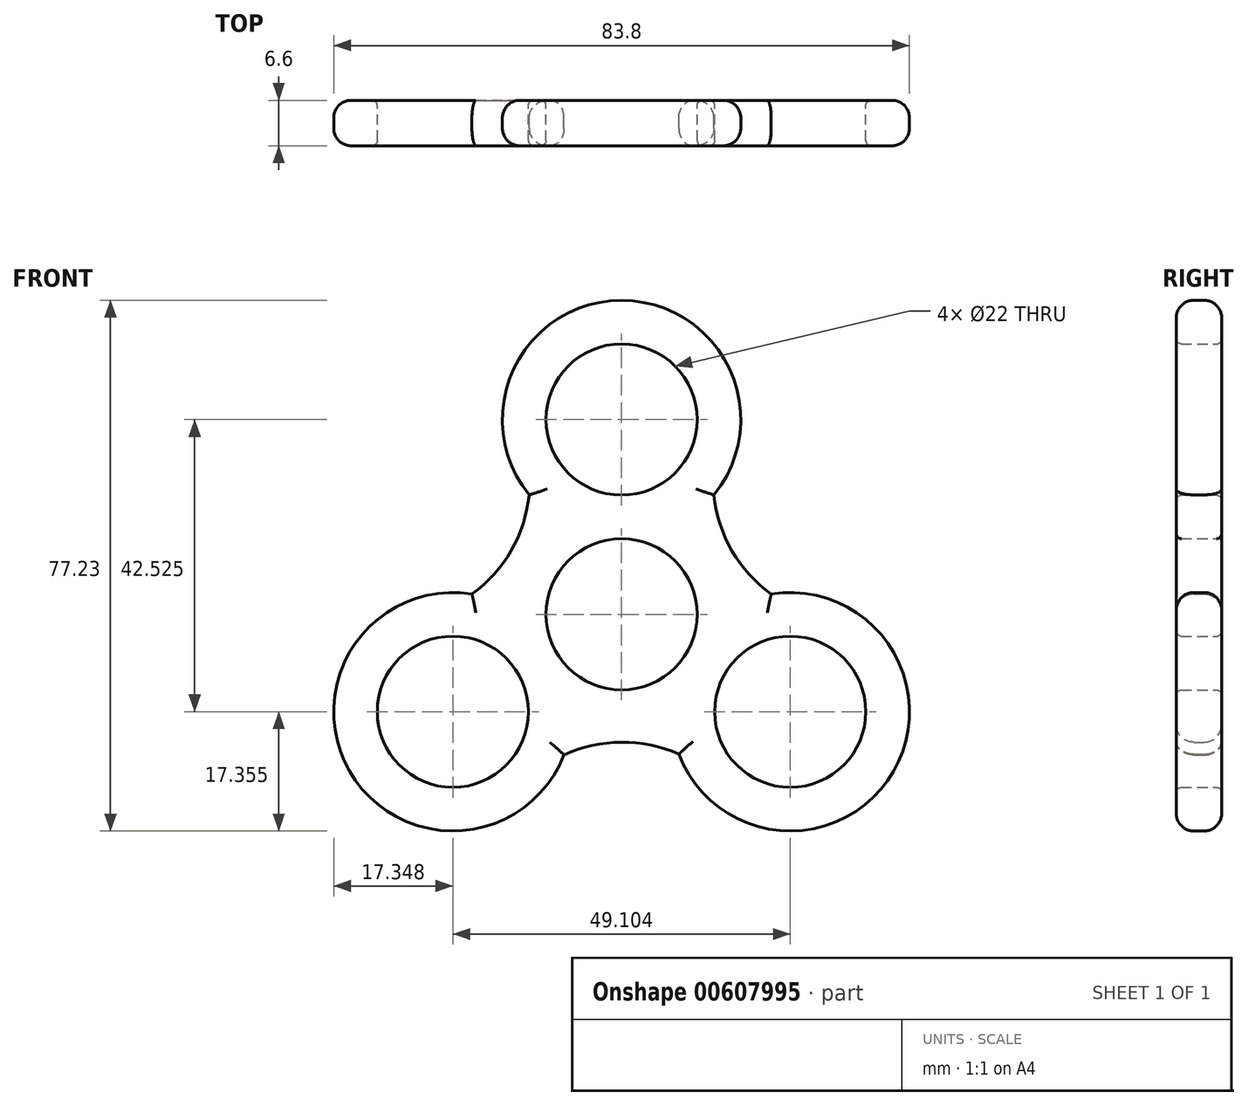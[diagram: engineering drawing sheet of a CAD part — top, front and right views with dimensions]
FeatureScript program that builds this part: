
annotation { "Feature Type Name" : "Feature", "Feature Type Description" : "" }
export const myFeature = defineFeature(function(context is Context, id is Id, definition is map)
    precondition{}
    {
        {
            var Q0;
            Q0=qCreatedBy(makeId("Front.planeOp"),FACE);
            var sketch = newSketch(context, id + "F0", { "sketchPlane" : qUnion([Q0])});
            skCircle(sketch, "E0", {"center": v(0, 0) * mm, "radius": 11 * mm});
            skCircle(sketch, "E1", {"center": v(0, 28.35) * mm, "radius": 11 * mm});
            skCircle(sketch, "E2", {"center": v(24.55, -14.17) * mm, "radius": 11 * mm});
            skCircle(sketch, "E3", {"center": v(-24.55, -14.18) * mm, "radius": 11 * mm});
            skArc(sketch, "E4", {"start": v(13.45, 17.39) * mm, "mid": v(0, 45.7) * mm, "end": v(-13.45, 17.39) * mm});
            skArc(sketch, "E5", {"start": v(8.33, -20.34) * mm, "mid": v(39.58, -22.85) * mm, "end": v(21.78, 2.95) * mm});
            skArc(sketch, "E6", {"start": v(-21.78, 2.95) * mm, "mid": v(-39.6, -22.8) * mm, "end": v(-8.38, -20.46) * mm});
            skPoint(sketch, "E7", {"position": v(13.45, 17.39) * mm});
            skPoint(sketch, "E8", {"position": v(21.78, 2.95) * mm});
            skPoint(sketch, "E9", {"position": v(8.33, -20.34) * mm});
            skPoint(sketch, "E10", {"position": v(-8.38, -20.46) * mm});
            skPoint(sketch, "E11", {"position": v(-21.78, 2.95) * mm});
            skPoint(sketch, "E12", {"position": v(-13.45, 17.39) * mm});
            skArc(sketch, "E13", {"start": v(13.45, 17.39) * mm, "mid": v(16.07, 9.28) * mm, "end": v(21.78, 2.95) * mm});
            skArc(sketch, "E14", {"start": v(8.33, -20.34) * mm, "mid": v(-0.03, -18.6) * mm, "end": v(-8.38, -20.46) * mm});
            skArc(sketch, "E15", {"start": v(-21.78, 2.95) * mm, "mid": v(-16.07, 9.28) * mm, "end": v(-13.45, 17.39) * mm});
            skPoint(sketch, "E16.orphan", {"position": v(-9.7, 13.96) * mm});
            skPoint(sketch, "E17.orphan", {"position": v(9.7, 13.96) * mm});
            skPoint(sketch, "E18.orphan", {"position": v(-7.24, -15.38) * mm});
            skPoint(sketch, "E19.orphan", {"position": v(-16.94, 1.42) * mm});
            skPoint(sketch, "E20.orphan", {"position": v(16.94, 1.42) * mm});
            skPoint(sketch, "E21.orphan", {"position": v(7.24, -15.38) * mm});
            skSolve(sketch);
        }
        {
            var Q0;
            Q0 = qSketchRegion(id + "F0", true);
            extrude(context, id + "F1", {"entities" : qUnion([Q0]), "depth" : 6.6 * mm, "offsetDistance" : 25.4 * mm});
        }
        {
            var Q0;
            Q0=makeQuery(id+"F1.opExtrude","CAP_EDGE",EDGE,{"disambiguationData":[OSD([sQuery(id+"F0.wireOp",EDGE,"E4")])],"isStart":false});
            var Q1;
            Q1=makeQuery(id+"F1.opExtrude","CAP_EDGE",EDGE,{"disambiguationData":[OSD([sQuery(id+"F0.wireOp",EDGE,"E4")])],"isStart":true});
            var Q2;
            Q2=makeQuery(id+"F1.opExtrude","CAP_EDGE",EDGE,{"disambiguationData":[OSD([sQuery(id+"F0.wireOp",EDGE,"E13")])],"isStart":false});
            var Q3;
            Q3=makeQuery(id+"F1.opExtrude","CAP_EDGE",EDGE,{"disambiguationData":[OSD([sQuery(id+"F0.wireOp",EDGE,"E15")])],"isStart":false});
            var Q4;
            Q4=makeQuery(id+"F1.opExtrude","CAP_EDGE",EDGE,{"disambiguationData":[OSD([sQuery(id+"F0.wireOp",EDGE,"E6")])],"isStart":false});
            var Q5;
            Q5=makeQuery(id+"F1.opExtrude","CAP_EDGE",EDGE,{"disambiguationData":[OSD([sQuery(id+"F0.wireOp",EDGE,"E14")])],"isStart":false});
            var Q6;
            Q6=makeQuery(id+"F1.opExtrude","CAP_EDGE",EDGE,{"disambiguationData":[OSD([sQuery(id+"F0.wireOp",EDGE,"E5")])],"isStart":false});
            var Q7;
            Q7=makeQuery(id+"F1.opExtrude","CAP_EDGE",EDGE,{"disambiguationData":[OSD([sQuery(id+"F0.wireOp",EDGE,"E13")])],"isStart":true});
            var Q8;
            Q8=makeQuery(id+"F1.opExtrude","CAP_EDGE",EDGE,{"disambiguationData":[OSD([sQuery(id+"F0.wireOp",EDGE,"E15")])],"isStart":true});
            var Q9;
            Q9=makeQuery(id+"F1.opExtrude","CAP_EDGE",EDGE,{"disambiguationData":[OSD([sQuery(id+"F0.wireOp",EDGE,"E6")])],"isStart":true});
            var Q10;
            Q10=makeQuery(id+"F1.opExtrude","CAP_EDGE",EDGE,{"disambiguationData":[OSD([sQuery(id+"F0.wireOp",EDGE,"E14")])],"isStart":true});
            var Q11;
            Q11=makeQuery(id+"F1.opExtrude","CAP_EDGE",EDGE,{"disambiguationData":[OSD([sQuery(id+"F0.wireOp",EDGE,"E5")])],"isStart":true});
            fillet(context, id + "F2", {"entities" : qUnion([Q0, Q1, Q2, Q3, Q4, Q5, Q6, Q7, Q8, Q9, Q10, Q11]), "radius" : 2.54 * mm, "tangentPropagation" : true, "allowEdgeOverflow" : false});
        }
        {
            var Q0;
            Q0=makeQuery(id+"F1.opExtrude","CAP_EDGE",EDGE,{"disambiguationData":[OSD([sQuery(id+"F0.wireOp",EDGE,"E0")])],"isStart":false});
            var Q1;
            Q1=makeQuery(id+"F1.opExtrude","CAP_EDGE",EDGE,{"disambiguationData":[OSD([sQuery(id+"F0.wireOp",EDGE,"E0")])],"isStart":true});
            var Q2;
            Q2=makeQuery(id+"F1.opExtrude","CAP_EDGE",EDGE,{"disambiguationData":[OSD([sQuery(id+"F0.wireOp",EDGE,"E2")])],"isStart":false});
            var Q3;
            Q3=makeQuery(id+"F1.opExtrude","CAP_EDGE",EDGE,{"disambiguationData":[OSD([sQuery(id+"F0.wireOp",EDGE,"E2")])],"isStart":true});
            var Q4;
            Q4=makeQuery(id+"F1.opExtrude","CAP_EDGE",EDGE,{"disambiguationData":[OSD([sQuery(id+"F0.wireOp",EDGE,"E3")])],"isStart":false});
            var Q5;
            Q5=makeQuery(id+"F1.opExtrude","CAP_EDGE",EDGE,{"disambiguationData":[OSD([sQuery(id+"F0.wireOp",EDGE,"E3")])],"isStart":true});
            var Q6;
            Q6=makeQuery(id+"F1.opExtrude","CAP_EDGE",EDGE,{"disambiguationData":[OSD([sQuery(id+"F0.wireOp",EDGE,"E1")])],"isStart":false});
            var Q7;
            Q7=makeQuery(id+"F1.opExtrude","CAP_EDGE",EDGE,{"disambiguationData":[OSD([sQuery(id+"F0.wireOp",EDGE,"E1")])],"isStart":true});
            fillet(context, id + "F3", {"entities" : qUnion([Q0, Q1, Q2, Q3, Q4, Q5, Q6, Q7]), "radius" : 0.76 * mm, "tangentPropagation" : true, "allowEdgeOverflow" : false});
        }
    });
